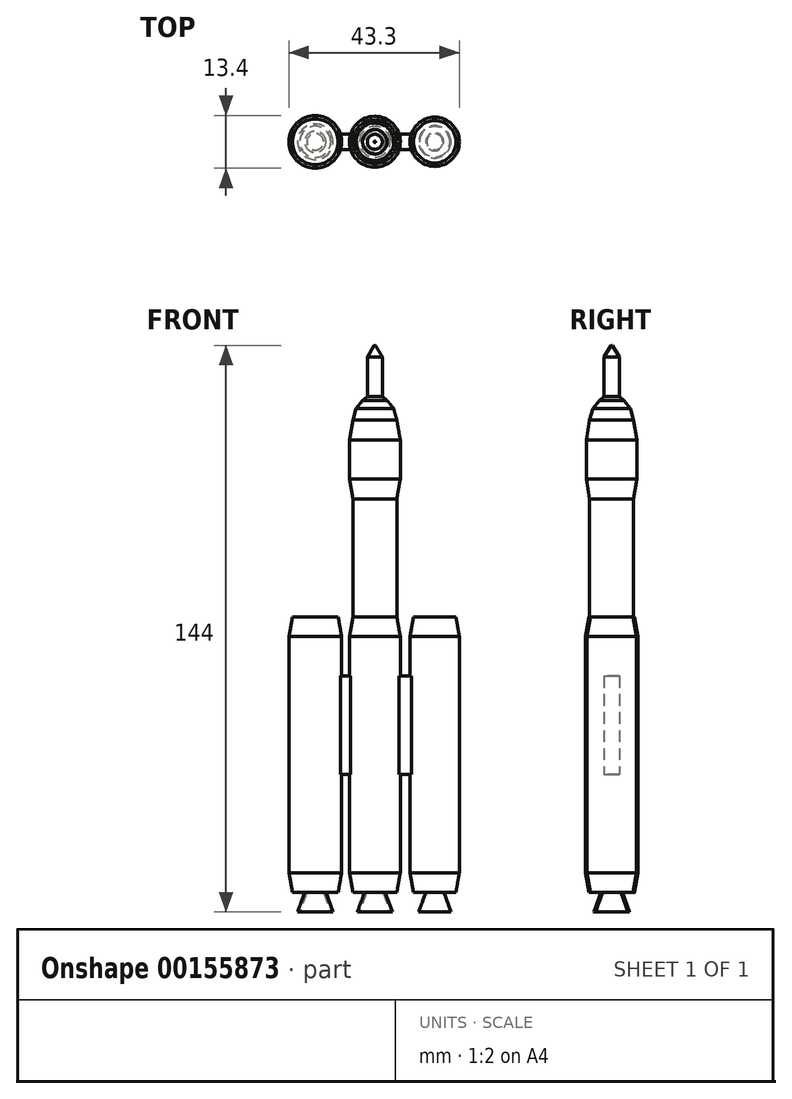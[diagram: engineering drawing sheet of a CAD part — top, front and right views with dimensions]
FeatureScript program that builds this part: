
annotation { "Feature Type Name" : "Feature", "Feature Type Description" : "" }
export const myFeature = defineFeature(function(context is Context, id is Id, definition is map)
    precondition{}
    {
        {
            var Q0;
            Q0=qCreatedBy(makeId("Top.planeOp"),FACE);
            var sketch = newSketch(context, id + "F0", { "sketchPlane" : qUnion([Q0])});
            skCircle(sketch, "E0", {"center": v(0, 0) * mm, "radius": 6.47 * mm});
            skSolve(sketch);
        }
        {
            var Q0;
            Q0=makeQuery(id+"F0.imprint","IMPRINT",FACE,{"disambiguationData":[TD([[makeQuery(id+"F0.imprint","IMPRINT",EDGE,{"derivedFrom":sQuery(id+"F0.wireOp",EDGE,"E0")}),1.0]])]});
            extrude(context, id + "F1", {"entities" : qUnion([Q0]), "depth" : 10 * mm, "hasSecondDirection" : true, "secondDirectionOppositeDirection" : true, "secondDirectionDepth" : 50 * mm});
        }
        {
            var Q0;
            Q0=makeQuery(id+"F1.opExtrude","CAP_FACE",FACE,{"disambiguationData":[OSD([sQuery(id+"F0.wireOp",EDGE,"E0")])],"isStart":false});
            extrude(context, id + "F2", {"entities" : qUnion([Q0]), "operationType" : NewBodyOperationType.ADD, "depth" : 5 * mm, "hasDraft" : true, "draftAngle" : 10 * degree, "draftPullDirection" : true});
        }
        {
            var Q0;
            Q0=makeQuery(id+"F1.opExtrude","CAP_FACE",FACE,{"disambiguationData":[OSD([sQuery(id+"F0.wireOp",EDGE,"E0")])],"isStart":true});
            extrude(context, id + "F3", {"entities" : qUnion([Q0]), "operationType" : NewBodyOperationType.ADD, "depth" : 5 * mm, "hasDraft" : true, "draftAngle" : 10 * degree, "draftPullDirection" : true});
        }
        {
            var Q0;
            Q0=makeQuery(id+"F3.opExtrude","CAP_FACE",FACE,{"disambiguationData":[OSD([sQuery(id+"F0.wireOp",EDGE,"E0")])],"isStart":false});
            var sketch = newSketch(context, id + "F4", { "sketchPlane" : qUnion([Q0])});
            skCircle(sketch, "E1", {"center": v(0, 0) * mm, "radius": 2.63 * mm});
            skSolve(sketch);
        }
        {
            var Q0;
            Q0=makeQuery(id+"F4.imprint","IMPRINT",FACE,{"disambiguationData":[TD([[makeQuery(id+"F4.imprint","IMPRINT",EDGE,{"derivedFrom":sQuery(id+"F4.wireOp",EDGE,"E1")}),1.0]])]});
            extrude(context, id + "F5", {"entities" : qUnion([Q0]), "operationType" : NewBodyOperationType.ADD, "depth" : 5 * mm, "hasDraft" : true, "draftAngle" : 20 * degree});
        }
        {
            var Q0;
            Q0=makeQuery(id+"F5.opExtrude","CAP_FACE",FACE,{"disambiguationData":[OSD([sQuery(id+"F4.wireOp",EDGE,"E1")])],"isStart":false});
            var sketch = newSketch(context, id + "F6", { "sketchPlane" : qUnion([Q0])});
            skCircle(sketch, "E2", {"center": v(0, 0) * mm, "radius": 3.89 * mm});
            skSolve(sketch);
        }
        {
            var Q0;
            Q0=makeQuery(id+"F6.imprint","IMPRINT",FACE,{"disambiguationData":[TD([[makeQuery(id+"F6.imprint","IMPRINT",EDGE,{"derivedFrom":sQuery(id+"F6.wireOp",EDGE,"E2")}),1.0]])]});
            extrude(context, id + "F7", {"entities" : qUnion([Q0]), "operationType" : NewBodyOperationType.REMOVE, "oppositeDirection" : true, "depth" : 5 * mm, "hasDraft" : true, "draftAngle" : 20 * degree, "draftPullDirection" : true});
        }
        {
            var Q0;
            Q0=qCreatedBy(makeId("Top.planeOp"),FACE);
            var sketch = newSketch(context, id + "F8", { "sketchPlane" : qUnion([Q0])});
            skLineSegment(sketch, "E3.bottom", {"start": v(0, 0) * mm, "end": v(-10.02, 0) * mm});
            skLineSegment(sketch, "E3.top", {"start": v(0, 1.91) * mm, "end": v(-10.02, 1.91) * mm});
            skLineSegment(sketch, "E3.left", {"start": v(0, 0) * mm, "end": v(0, 1.91) * mm});
            skLineSegment(sketch, "E3.right", {"start": v(-10.02, 0) * mm, "end": v(-10.02, 1.91) * mm});
            skLineSegment(sketch, "E4.bottom", {"start": v(0, 0) * mm, "end": v(10.08, 0) * mm});
            skLineSegment(sketch, "E4.top", {"start": v(0, 1.91) * mm, "end": v(10.08, 1.91) * mm});
            skLineSegment(sketch, "E4.right", {"start": v(10.08, 0) * mm, "end": v(10.08, 1.91) * mm});
            skLineSegment(sketch, "E5.top", {"start": v(0, -2) * mm, "end": v(-10.02, -2) * mm});
            skLineSegment(sketch, "E5.left", {"start": v(0, 0) * mm, "end": v(0, -2) * mm});
            skLineSegment(sketch, "E5.right", {"start": v(-10.02, 0) * mm, "end": v(-10.02, -2) * mm});
            skLineSegment(sketch, "E6.bottom", {"start": v(0, -2) * mm, "end": v(10.08, -2) * mm});
            skLineSegment(sketch, "E6.left", {"start": v(0, -2) * mm, "end": v(0, 0) * mm});
            skLineSegment(sketch, "E6.right", {"start": v(10.08, -2) * mm, "end": v(10.08, 0) * mm});
            skSolve(sketch);
        }
        {
            var Q0;
            Q0 = qSketchRegion(id + "F8", true);
            extrude(context, id + "F9", {"entities" : qUnion([Q0]), "operationType" : NewBodyOperationType.ADD, "oppositeDirection" : true, "depth" : 25 * mm});
        }
        {
            var Q0;
            {var subQ0=sQuery(id+"F8.wireOp",EDGE,"E6.right");var subQ1=sQuery(id+"F8.wireOp",EDGE,"E4.right");var subQ2=sQuery(id+"F8.wireOp",EDGE,"E6.bottom");var subQ3=sQuery(id+"F8.wireOp",EDGE,"E5.top");var subQ4=sQuery(id+"F8.wireOp",EDGE,"E4.top");var subQ5=sQuery(id+"F8.wireOp",EDGE,"E3.top");Q0=makeQuery(id+"F9.boolean.opBoolean","SPLIT",FACE,{"disambiguationData":[TD([makeQuery(id+"F9.opExtrude","SWEPT_FACE",FACE,{"disambiguationData":[OSD([subQ1,subQ0])]})])],"derivedFrom":makeQuery(id+"F9.opExtrude","CAP_FACE",FACE,{"disambiguationData":[OSD([subQ5,sQuery(id+"F8.wireOp",EDGE,"E3.right"),subQ4,subQ1,subQ3,sQuery(id+"F8.wireOp",EDGE,"E5.right"),subQ2,subQ0])],"isStart":true})});}
            var sketch = newSketch(context, id + "F10", { "sketchPlane" : qUnion([Q0])});
            skCircle(sketch, "E7", {"center": v(15.23, 0) * mm, "radius": 6.26 * mm});
            skSolve(sketch);
        }
        {
            var Q0;
            {var subQ2=sQuery(id+"F8.wireOp",EDGE,"E6.right");var subQ3=sQuery(id+"F8.wireOp",EDGE,"E4.right");var subQ14=makeQuery(id+"F9.opExtrude","CAP_EDGE",EDGE,{"disambiguationData":[OSD([subQ3,subQ2])],"isStart":true});Q0=makeQuery(id+"F10.imprint","IMPRINT",FACE,{"disambiguationData":[TD([[makeQuery(id+"F10.imprint","IMPRINT",EDGE,{"derivedFrom":subQ14}),-1.0]])]});}
            var Q1;
            Q1 = qSketchRegion(id + "F10", true);
            extrude(context, id + "F11", {"entities" : qUnion([Q0, Q1]), "operationType" : NewBodyOperationType.ADD, "depth" : 10 * mm, "hasSecondDirection" : true, "secondDirectionOppositeDirection" : true, "secondDirectionDepth" : 50 * mm});
        }
        {
            var Q0;
            Q0=makeQuery(id+"F11.opExtrude","CAP_FACE",FACE,{"disambiguationData":[OSD([sQuery(id+"F10.wireOp",EDGE,"E7")])],"isStart":false});
            extrude(context, id + "F12", {"entities" : qUnion([Q0]), "operationType" : NewBodyOperationType.ADD, "depth" : 5 * mm, "hasDraft" : true, "draftAngle" : 10 * degree, "draftPullDirection" : true});
        }
        {
            var Q0;
            Q0=makeQuery(id+"F11.opExtrude","CAP_FACE",FACE,{"disambiguationData":[OSD([sQuery(id+"F10.wireOp",EDGE,"E7")])],"isStart":true});
            extrude(context, id + "F13", {"entities" : qUnion([Q0]), "operationType" : NewBodyOperationType.ADD, "depth" : 5 * mm, "hasDraft" : true, "draftAngle" : 10 * degree, "draftPullDirection" : true});
        }
        {
            var Q0;
            Q0=makeQuery(id+"F13.opExtrude","CAP_FACE",FACE,{"disambiguationData":[OSD([sQuery(id+"F10.wireOp",EDGE,"E7")])],"isStart":false});
            var sketch = newSketch(context, id + "F14", { "sketchPlane" : qUnion([Q0])});
            skCircle(sketch, "E8", {"center": v(15.23, 0) * mm, "radius": 2.3 * mm});
            skSolve(sketch);
        }
        {
            var Q0;
            Q0=makeQuery(id+"F14.imprint","IMPRINT",FACE,{"disambiguationData":[TD([[makeQuery(id+"F14.imprint","IMPRINT",EDGE,{"derivedFrom":sQuery(id+"F14.wireOp",EDGE,"E8")}),1.0]])]});
            extrude(context, id + "F15", {"entities" : qUnion([Q0]), "operationType" : NewBodyOperationType.ADD, "depth" : 5 * mm, "hasDraft" : true, "draftAngle" : 20 * degree});
        }
        {
            var Q0;
            Q0=makeQuery(id+"F15.opExtrude","CAP_FACE",FACE,{"disambiguationData":[OSD([sQuery(id+"F14.wireOp",EDGE,"E8")])],"isStart":false});
            var sketch = newSketch(context, id + "F16", { "sketchPlane" : qUnion([Q0])});
            skCircle(sketch, "E9", {"center": v(15.23, 0) * mm, "radius": 3.86 * mm});
            skSolve(sketch);
        }
        {
            var Q0;
            Q0=makeQuery(id+"F16.imprint","IMPRINT",FACE,{"disambiguationData":[TD([[makeQuery(id+"F16.imprint","IMPRINT",EDGE,{"derivedFrom":sQuery(id+"F16.wireOp",EDGE,"E9")}),1.0]])]});
            extrude(context, id + "F17", {"entities" : qUnion([Q0]), "operationType" : NewBodyOperationType.REMOVE, "oppositeDirection" : true, "depth" : 5 * mm, "hasDraft" : true, "draftAngle" : 20 * degree, "draftPullDirection" : true});
        }
        {
            var Q0;
            {var subQ0=sQuery(id+"F8.wireOp",EDGE,"E6.bottom");var subQ1=sQuery(id+"F8.wireOp",EDGE,"E5.top");var subQ2=sQuery(id+"F8.wireOp",EDGE,"E4.top");var subQ3=sQuery(id+"F8.wireOp",EDGE,"E3.top");var subQ4=sQuery(id+"F8.wireOp",EDGE,"E5.right");var subQ5=sQuery(id+"F8.wireOp",EDGE,"E3.right");Q0=makeQuery(id+"F9.boolean.opBoolean","SPLIT",FACE,{"disambiguationData":[TD([makeQuery(id+"F9.opExtrude","SWEPT_FACE",FACE,{"disambiguationData":[OSD([subQ5,subQ4])]})])],"derivedFrom":makeQuery(id+"F9.opExtrude","CAP_FACE",FACE,{"disambiguationData":[OSD([subQ3,subQ5,subQ2,sQuery(id+"F8.wireOp",EDGE,"E4.right"),subQ1,subQ4,subQ0,sQuery(id+"F8.wireOp",EDGE,"E6.right")])],"isStart":true})});}
            var sketch = newSketch(context, id + "F18", { "sketchPlane" : qUnion([Q0])});
            skCircle(sketch, "E10", {"center": v(-15.13, 0) * mm, "radius": 6.7 * mm});
            skSolve(sketch);
        }
        {
            var Q0;
            {var subQ3=sQuery(id+"F8.wireOp",EDGE,"E5.right");var subQ6=sQuery(id+"F8.wireOp",EDGE,"E3.right");var subQ14=makeQuery(id+"F9.opExtrude","CAP_EDGE",EDGE,{"disambiguationData":[OSD([subQ6,subQ3])],"isStart":true});Q0=makeQuery(id+"F18.imprint","IMPRINT",FACE,{"disambiguationData":[TD([[makeQuery(id+"F18.imprint","IMPRINT",EDGE,{"derivedFrom":subQ14}),1.0]])]});}
            var Q1;
            Q1 = qSketchRegion(id + "F18", true);
            extrude(context, id + "F19", {"entities" : qUnion([Q0, Q1]), "operationType" : NewBodyOperationType.ADD, "depth" : 10 * mm, "hasSecondDirection" : true, "secondDirectionOppositeDirection" : true, "secondDirectionDepth" : 50 * mm});
        }
        {
            var Q0;
            Q0=makeQuery(id+"F19.opExtrude","CAP_FACE",FACE,{"disambiguationData":[OSD([sQuery(id+"F18.wireOp",EDGE,"E10")])],"isStart":false});
            extrude(context, id + "F20", {"entities" : qUnion([Q0]), "operationType" : NewBodyOperationType.ADD, "depth" : 5 * mm, "hasDraft" : true, "draftAngle" : 10 * degree, "draftPullDirection" : true});
        }
        {
            var Q0;
            Q0=makeQuery(id+"F19.opExtrude","CAP_FACE",FACE,{"disambiguationData":[OSD([sQuery(id+"F18.wireOp",EDGE,"E10")])],"isStart":true});
            extrude(context, id + "F21", {"entities" : qUnion([Q0]), "operationType" : NewBodyOperationType.ADD, "depth" : 5 * mm, "hasDraft" : true, "draftAngle" : 10 * degree, "draftPullDirection" : true});
        }
        {
            var Q0;
            Q0=makeQuery(id+"F21.opExtrude","CAP_FACE",FACE,{"disambiguationData":[OSD([sQuery(id+"F18.wireOp",EDGE,"E10")])],"isStart":false});
            var sketch = newSketch(context, id + "F22", { "sketchPlane" : qUnion([Q0])});
            skCircle(sketch, "E11", {"center": v(-15.13, 0) * mm, "radius": 2.7 * mm});
            skSolve(sketch);
        }
        {
            var Q0;
            Q0=makeQuery(id+"F22.imprint","IMPRINT",FACE,{"disambiguationData":[TD([[makeQuery(id+"F22.imprint","IMPRINT",EDGE,{"derivedFrom":sQuery(id+"F22.wireOp",EDGE,"E11")}),1.0]])]});
            extrude(context, id + "F23", {"entities" : qUnion([Q0]), "operationType" : NewBodyOperationType.ADD, "depth" : 5 * mm, "hasDraft" : true, "draftAngle" : 20 * degree});
        }
        {
            var Q0;
            Q0=makeQuery(id+"F23.opExtrude","CAP_FACE",FACE,{"disambiguationData":[OSD([sQuery(id+"F22.wireOp",EDGE,"E11")])],"isStart":false});
            var sketch = newSketch(context, id + "F24", { "sketchPlane" : qUnion([Q0])});
            skCircle(sketch, "E12", {"center": v(-15.13, 0) * mm, "radius": 3.95 * mm});
            skSolve(sketch);
        }
        {
            var Q0;
            Q0=makeQuery(id+"F24.imprint","IMPRINT",FACE,{"disambiguationData":[TD([[makeQuery(id+"F24.imprint","IMPRINT",EDGE,{"derivedFrom":sQuery(id+"F24.wireOp",EDGE,"E12")}),1.0]])]});
            extrude(context, id + "F25", {"entities" : qUnion([Q0]), "operationType" : NewBodyOperationType.REMOVE, "oppositeDirection" : true, "depth" : 5 * mm, "hasDraft" : true, "draftAngle" : 20 * degree, "draftPullDirection" : true});
        }
        {
            var Q0;
            Q0=makeQuery(id+"F2.opExtrude","CAP_FACE",FACE,{"disambiguationData":[OSD([sQuery(id+"F0.wireOp",EDGE,"E0")])],"isStart":false});
            extrude(context, id + "F26", {"entities" : qUnion([Q0]), "operationType" : NewBodyOperationType.ADD, "depth" : 30 * mm});
        }
        {
            var Q0;
            Q0=makeQuery(id+"F26.opExtrude","CAP_FACE",FACE,{"disambiguationData":[OSD([sQuery(id+"F0.wireOp",EDGE,"E0")])],"isStart":false});
            extrude(context, id + "F27", {"entities" : qUnion([Q0]), "operationType" : NewBodyOperationType.ADD, "depth" : 5 * mm, "hasDraft" : true, "draftAngle" : 10 * degree});
        }
        {
            var Q0;
            Q0=makeQuery(id+"F27.opExtrude","CAP_FACE",FACE,{"disambiguationData":[OSD([sQuery(id+"F0.wireOp",EDGE,"E0")])],"isStart":false});
            extrude(context, id + "F28", {"entities" : qUnion([Q0]), "operationType" : NewBodyOperationType.ADD, "depth" : 10 * mm});
        }
        {
            var Q0;
            Q0=makeQuery(id+"F28.opExtrude","CAP_FACE",FACE,{"disambiguationData":[OSD([sQuery(id+"F0.wireOp",EDGE,"E0")])],"isStart":false});
            extrude(context, id + "F29", {"entities" : qUnion([Q0]), "operationType" : NewBodyOperationType.ADD, "depth" : 5 * mm, "hasDraft" : true, "draftAngle" : 10 * degree, "draftPullDirection" : true});
        }
        {
            var Q0;
            Q0=makeQuery(id+"F29.opExtrude","CAP_FACE",FACE,{"disambiguationData":[OSD([sQuery(id+"F0.wireOp",EDGE,"E0")])],"isStart":false});
            extrude(context, id + "F30", {"entities" : qUnion([Q0]), "operationType" : NewBodyOperationType.ADD, "depth" : 3 * mm, "hasDraft" : true, "draftAngle" : 15 * degree, "draftPullDirection" : true});
        }
        {
            var Q0;
            Q0=makeQuery(id+"F30.opExtrude","CAP_FACE",FACE,{"disambiguationData":[OSD([sQuery(id+"F0.wireOp",EDGE,"E0")])],"isStart":false});
            extrude(context, id + "F31", {"entities" : qUnion([Q0]), "operationType" : NewBodyOperationType.ADD, "depth" : 2 * mm, "hasDraft" : true, "draftAngle" : 40 * degree, "draftPullDirection" : true});
        }
        {
            var Q0;
            Q0=makeQuery(id+"F31.opExtrude","CAP_FACE",FACE,{"disambiguationData":[OSD([sQuery(id+"F0.wireOp",EDGE,"E0")])],"isStart":false});
            extrude(context, id + "F32", {"entities" : qUnion([Q0]), "operationType" : NewBodyOperationType.ADD, "depth" : 1 * mm, "hasDraft" : true, "draftAngle" : 50 * degree, "draftPullDirection" : true});
        }
        {
            var Q0;
            Q0=makeQuery(id+"F32.opExtrude","CAP_FACE",FACE,{"disambiguationData":[OSD([sQuery(id+"F0.wireOp",EDGE,"E0")])],"isStart":false});
            extrude(context, id + "F33", {"entities" : qUnion([Q0]), "operationType" : NewBodyOperationType.ADD, "depth" : 10 * mm});
        }
        {
            var Q0;
            Q0=makeQuery(id+"F33.opExtrude","CAP_FACE",FACE,{"disambiguationData":[OSD([sQuery(id+"F0.wireOp",EDGE,"E0")])],"isStart":false});
            extrude(context, id + "F34", {"entities" : qUnion([Q0]), "operationType" : NewBodyOperationType.ADD, "depth" : 3 * mm, "hasDraft" : true, "draftAngle" : 30 * degree, "draftPullDirection" : true});
        }
    });
